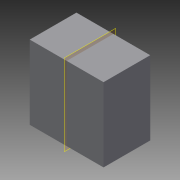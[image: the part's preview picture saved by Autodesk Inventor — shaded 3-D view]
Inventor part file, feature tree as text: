
AUTODESK INVENTOR PART (.ipt)
format: ipt  version: 2014 (Build 180170000, 170)  size: 71,680 bytes
history: native  units: mm
features: extrude x1, plane x1, sketch x1
ambient origin geometry x8: Origin, YZ Plane, XZ Plane, XY Plane, X Axis, Y Axis, Z Axis, Center Point
bodies: Volumenkörper1 (feature_tree)
feature tree (3):
  extrude  "Extrusion1"  Depth=7.9mm
  plane  "Arbeitsebene1"
  sketch  "Skizze1"  dims[d0=7.9mm d1=7.9mm d2=5.0mm d3=0.0mm]
